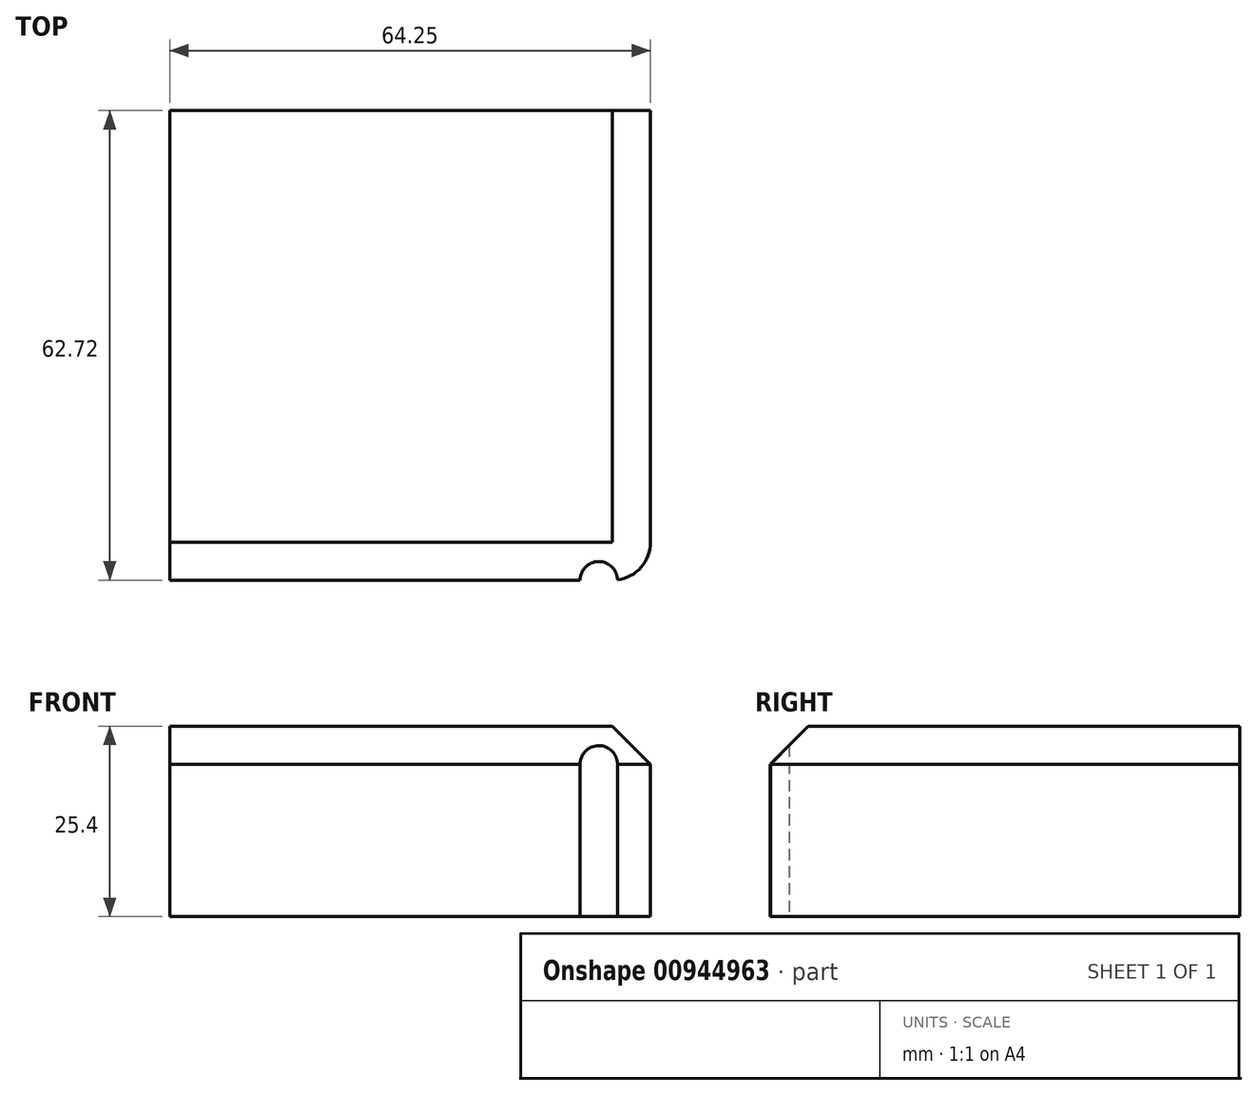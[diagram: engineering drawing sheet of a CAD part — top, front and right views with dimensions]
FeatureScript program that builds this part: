
annotation { "Feature Type Name" : "Feature", "Feature Type Description" : "" }
export const myFeature = defineFeature(function(context is Context, id is Id, definition is map)
    precondition{}
    {
        {
            var Q0;
            Q0=qCreatedBy(makeId("Top.planeOp"),FACE);
            var sketch = newSketch(context, id + "F0", { "sketchPlane" : qUnion([Q0])});
            skLineSegment(sketch, "E0.bottom", {"start": v(0, 0) * mm, "end": v(-64.25, 0) * mm});
            skLineSegment(sketch, "E0.top", {"start": v(0, 62.72) * mm, "end": v(-64.25, 62.72) * mm});
            skLineSegment(sketch, "E0.left", {"start": v(0, 0) * mm, "end": v(0, 62.72) * mm});
            skLineSegment(sketch, "E0.right", {"start": v(-64.25, 0) * mm, "end": v(-64.25, 62.72) * mm});
            skSolve(sketch);
        }
        {
            var Q0;
            Q0=qCreatedBy(makeId("Top.planeOp"),FACE);
            var sketch = newSketch(context, id + "F1", { "sketchPlane" : qUnion([Q0])});
            skPoint(sketch, "E1", {"position": v(-6.92, 0) * mm});
            skSolve(sketch);
        }
        {
            var Q0;
            Q0 = qSketchRegion(id + "F0", true);
            extrude(context, id + "F2", {"entities" : qUnion([Q0]), "depth" : 25.4 * mm, "offsetDistance" : 25.4 * mm});
        }
        {
            var Q0;
            Q0=makeQuery(id+"F2.opExtrude","SWEPT_EDGE",EDGE,{"disambiguationData":[OSD([sQuery(id+"F0.wireOp",EDGE,"E0.bottom"),sQuery(id+"F0.wireOp",EDGE,"E0.left")])]});
            fillet(context, id + "F3", {"entities" : qUnion([Q0]), "radius" : 5.08 * mm, "tangentPropagation" : true, "allowEdgeOverflow" : false});
        }
        {
            var Q0;
            Q0=makeQuery(id+"F2.opExtrude","CAP_EDGE",EDGE,{"disambiguationData":[OSD([sQuery(id+"F0.wireOp",EDGE,"E0.left")])],"isStart":false});
            chamfer(context, id + "F4", {"entities" : qUnion([Q0]), "width" : 5.08 * mm, "tangentPropagation" : true});
        }
        {
            var Q0;
            Q0=sQuery(id+"F1.wireOp",VERTEX,"E1");
            var Q1;
            Q1=makeQuery(id+"F2.opExtrude","SWEPT_BODY",BODY,{"disambiguationData":[OSD([sQuery(id+"F0.wireOp",EDGE,"E0.bottom"),sQuery(id+"F0.wireOp",EDGE,"E0.top"),sQuery(id+"F0.wireOp",EDGE,"E0.left"),sQuery(id+"F0.wireOp",EDGE,"E0.right")])]});
            hole(context, id + "F5", {"style" : HoleStyle.SIMPLE, "endStyle" : HoleEndStyle.THROUGH, "oppositeDirection" : true, "holeDiameter" : 5 * mm, "majorDiameter" : 5 * mm, "isTappedThrough" : true, "tappedDepth" : 12 * mm, "tapClearance" : 3, "locations" : qUnion([Q0]), "scope" : qUnion([Q1])});
        }
    });
